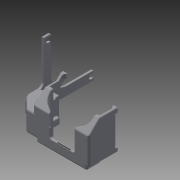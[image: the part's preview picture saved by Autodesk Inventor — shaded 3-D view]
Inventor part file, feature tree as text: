
AUTODESK INVENTOR PART (.ipt)
format: ipt  version: 2014 (Build 180170000, 170)  size: 1,110,528 bytes
history: native  units: in
note: dims shown in document units (in); Inventor stores cm internally (conversion verified against a paired STEP export)
features: fillet x5, extrude x4, sketch x4, other x1, imported_body x1
ambient origin geometry x8: Origin, YZ Plane, XZ Plane, XY Plane, X Axis, Y Axis, Z Axis, Center Point
bodies: Solid1 (feature_tree)
feature tree (15):
  other  "uploads-a6-b2-57-75-86-ReplicatorFanDuct21"
  extrude  "Extrusion1"  Depth=0.1in TaperAngle=0.0deg
  fillet  "Fillet1"  Radius=0.1969in
  extrude  "Extrusion2"  Depth=1.5748in
  fillet  "Fillet2"  Radius=0.1in
  extrude  "Extrusion4"  Depth=0.315in
  fillet  "Fillet3"  Radius=1.5748in
  extrude  "Extrusion5"  Depth=0.5906in
  fillet  "Fillet4"  Radius=0.1575in
  fillet  "Fillet5"  Radius=0.0787in
  imported_body  "Base1"
  sketch  "Sketch1"  dims[d0=0.4331in d1=0.1in d2=0.0in d3=0.1969in]
  sketch  "Sketch2"  dims[d4=0.2756in d5=1.5748in d6=0.1in d7=0.0in]
  sketch  "Sketch4"  dims[d8=0.1575in d13=0.315in d14=1.5748in]
  sketch  "Sketch6"  dims[d15=0.1in d16=0.0in d17=0.5906in d19=0.1575in d20=0.0787in d21=0.0787in d22=0.0787in d23=0.1969in d24=0.1969in d25=0.1in d26=0.0in d27=0.0394in d28=0.0394in]
